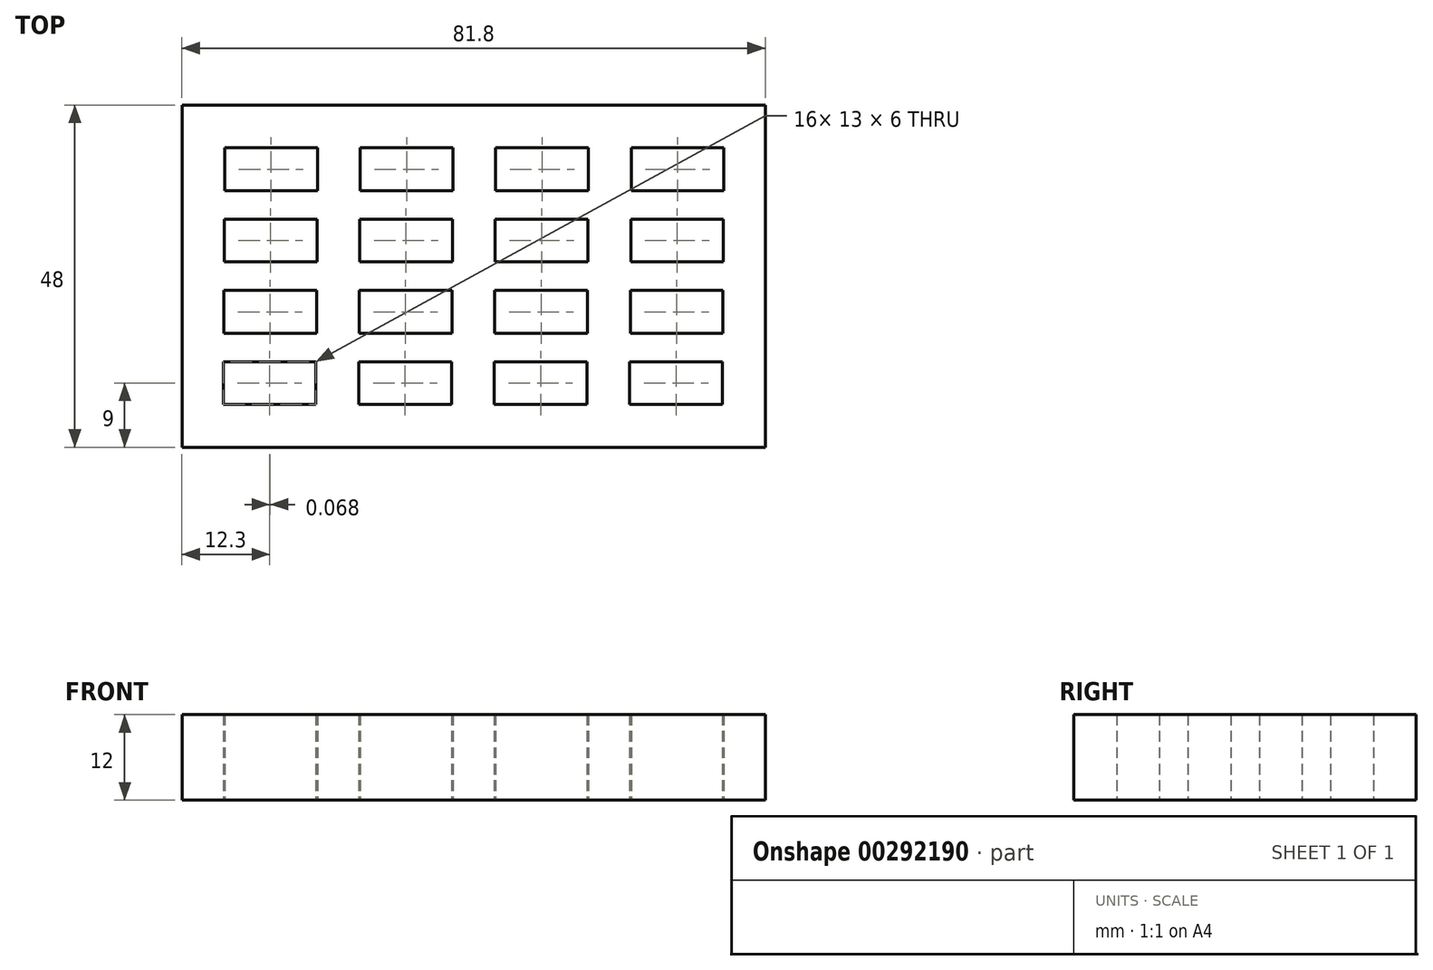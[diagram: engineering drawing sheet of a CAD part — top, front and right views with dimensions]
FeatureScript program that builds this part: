
annotation { "Feature Type Name" : "Feature", "Feature Type Description" : "" }
export const myFeature = defineFeature(function(context is Context, id is Id, definition is map)
    precondition{}
    {
        {
            var Q0;
            Q0=qCreatedBy(makeId("Top.planeOp"),FACE);
            var sketch = newSketch(context, id + "F0", { "sketchPlane" : qUnion([Q0])});
            skLineSegment(sketch, "E0.bottom", {"start": v(6.5, 3) * mm, "end": v(-6.5, 3) * mm});
            skLineSegment(sketch, "E0.top", {"start": v(6.5, -3) * mm, "end": v(-6.5, -3) * mm});
            skLineSegment(sketch, "E0.left", {"start": v(6.5, 3) * mm, "end": v(6.5, -3) * mm});
            skLineSegment(sketch, "E0.right", {"start": v(-6.5, 3) * mm, "end": v(-6.5, -3) * mm});
            skPoint(sketch, "E0.middle", {"position": v(0, 0) * mm});
            skLineSegment(sketch, "E1.0.1.0", {"start": v(6.57, 13) * mm, "end": v(-6.43, 13) * mm});
            skLineSegment(sketch, "E1.0.1.1", {"start": v(-6.43, 13) * mm, "end": v(-6.43, 7) * mm});
            skLineSegment(sketch, "E1.0.1.2", {"start": v(6.57, 7) * mm, "end": v(-6.43, 7) * mm});
            skLineSegment(sketch, "E1.0.1.3", {"start": v(6.57, 13) * mm, "end": v(6.57, 7) * mm});
            skPoint(sketch, "E1.0.1.4", {"position": v(0.07, 10) * mm});
            skLineSegment(sketch, "E1.0.2.0", {"start": v(6.64, 23) * mm, "end": v(-6.36, 23) * mm});
            skLineSegment(sketch, "E1.0.2.1", {"start": v(-6.36, 23) * mm, "end": v(-6.36, 17) * mm});
            skLineSegment(sketch, "E1.0.2.2", {"start": v(6.64, 17) * mm, "end": v(-6.36, 17) * mm});
            skLineSegment(sketch, "E1.0.2.3", {"start": v(6.64, 23) * mm, "end": v(6.64, 17) * mm});
            skPoint(sketch, "E1.0.2.4", {"position": v(0.14, 20) * mm});
            skLineSegment(sketch, "E1.0.3.0", {"start": v(6.7, 33) * mm, "end": v(-6.3, 33) * mm});
            skLineSegment(sketch, "E1.0.3.1", {"start": v(-6.3, 33) * mm, "end": v(-6.3, 27) * mm});
            skLineSegment(sketch, "E1.0.3.2", {"start": v(6.7, 27) * mm, "end": v(-6.3, 27) * mm});
            skLineSegment(sketch, "E1.0.3.3", {"start": v(6.7, 33) * mm, "end": v(6.7, 27) * mm});
            skPoint(sketch, "E1.0.3.4", {"position": v(0.2, 30) * mm});
            skLineSegment(sketch, "E1.1.0.0", {"start": v(25.5, 3) * mm, "end": v(12.5, 3) * mm});
            skLineSegment(sketch, "E1.1.0.1", {"start": v(12.5, 3) * mm, "end": v(12.5, -3) * mm});
            skLineSegment(sketch, "E1.1.0.2", {"start": v(25.5, -3) * mm, "end": v(12.5, -3) * mm});
            skLineSegment(sketch, "E1.1.0.3", {"start": v(25.5, 3) * mm, "end": v(25.5, -3) * mm});
            skPoint(sketch, "E1.1.0.4", {"position": v(19, 0) * mm});
            skLineSegment(sketch, "E1.1.1.0", {"start": v(25.57, 13) * mm, "end": v(12.57, 13) * mm});
            skLineSegment(sketch, "E1.1.1.1", {"start": v(12.57, 13) * mm, "end": v(12.57, 7) * mm});
            skLineSegment(sketch, "E1.1.1.2", {"start": v(25.57, 7) * mm, "end": v(12.57, 7) * mm});
            skLineSegment(sketch, "E1.1.1.3", {"start": v(25.57, 13) * mm, "end": v(25.57, 7) * mm});
            skPoint(sketch, "E1.1.1.4", {"position": v(19.07, 10) * mm});
            skLineSegment(sketch, "E1.1.2.0", {"start": v(25.64, 23) * mm, "end": v(12.64, 23) * mm});
            skLineSegment(sketch, "E1.1.2.1", {"start": v(12.64, 23) * mm, "end": v(12.64, 17) * mm});
            skLineSegment(sketch, "E1.1.2.2", {"start": v(25.64, 17) * mm, "end": v(12.64, 17) * mm});
            skLineSegment(sketch, "E1.1.2.3", {"start": v(25.64, 23) * mm, "end": v(25.64, 17) * mm});
            skPoint(sketch, "E1.1.2.4", {"position": v(19.14, 20) * mm});
            skLineSegment(sketch, "E1.1.3.0", {"start": v(25.7, 33) * mm, "end": v(12.7, 33) * mm});
            skLineSegment(sketch, "E1.1.3.1", {"start": v(12.7, 33) * mm, "end": v(12.7, 27) * mm});
            skLineSegment(sketch, "E1.1.3.2", {"start": v(25.7, 27) * mm, "end": v(12.7, 27) * mm});
            skLineSegment(sketch, "E1.1.3.3", {"start": v(25.7, 33) * mm, "end": v(25.7, 27) * mm});
            skPoint(sketch, "E1.1.3.4", {"position": v(19.2, 30) * mm});
            skLineSegment(sketch, "E1.2.0.0", {"start": v(44.5, 3) * mm, "end": v(31.5, 3) * mm});
            skLineSegment(sketch, "E1.2.0.1", {"start": v(31.5, 3) * mm, "end": v(31.5, -3) * mm});
            skLineSegment(sketch, "E1.2.0.2", {"start": v(44.5, -3) * mm, "end": v(31.5, -3) * mm});
            skLineSegment(sketch, "E1.2.0.3", {"start": v(44.5, 3) * mm, "end": v(44.5, -3) * mm});
            skPoint(sketch, "E1.2.0.4", {"position": v(38, 0) * mm});
            skLineSegment(sketch, "E1.2.1.0", {"start": v(44.57, 13) * mm, "end": v(31.57, 13) * mm});
            skLineSegment(sketch, "E1.2.1.1", {"start": v(31.57, 13) * mm, "end": v(31.57, 7) * mm});
            skLineSegment(sketch, "E1.2.1.2", {"start": v(44.57, 7) * mm, "end": v(31.57, 7) * mm});
            skLineSegment(sketch, "E1.2.1.3", {"start": v(44.57, 13) * mm, "end": v(44.57, 7) * mm});
            skPoint(sketch, "E1.2.1.4", {"position": v(38.07, 10) * mm});
            skLineSegment(sketch, "E1.2.2.0", {"start": v(44.64, 23) * mm, "end": v(31.64, 23) * mm});
            skLineSegment(sketch, "E1.2.2.1", {"start": v(31.64, 23) * mm, "end": v(31.64, 17) * mm});
            skLineSegment(sketch, "E1.2.2.2", {"start": v(44.64, 17) * mm, "end": v(31.64, 17) * mm});
            skLineSegment(sketch, "E1.2.2.3", {"start": v(44.64, 23) * mm, "end": v(44.64, 17) * mm});
            skPoint(sketch, "E1.2.2.4", {"position": v(38.14, 20) * mm});
            skLineSegment(sketch, "E1.2.3.0", {"start": v(44.7, 33) * mm, "end": v(31.7, 33) * mm});
            skLineSegment(sketch, "E1.2.3.1", {"start": v(31.7, 33) * mm, "end": v(31.7, 27) * mm});
            skLineSegment(sketch, "E1.2.3.2", {"start": v(44.7, 27) * mm, "end": v(31.7, 27) * mm});
            skLineSegment(sketch, "E1.2.3.3", {"start": v(44.7, 33) * mm, "end": v(44.7, 27) * mm});
            skPoint(sketch, "E1.2.3.4", {"position": v(38.2, 30) * mm});
            skLineSegment(sketch, "E1.3.0.0", {"start": v(63.5, 3) * mm, "end": v(50.5, 3) * mm});
            skLineSegment(sketch, "E1.3.0.1", {"start": v(50.5, 3) * mm, "end": v(50.5, -3) * mm});
            skLineSegment(sketch, "E1.3.0.2", {"start": v(63.5, -3) * mm, "end": v(50.5, -3) * mm});
            skLineSegment(sketch, "E1.3.0.3", {"start": v(63.5, 3) * mm, "end": v(63.5, -3) * mm});
            skPoint(sketch, "E1.3.0.4", {"position": v(57, 0) * mm});
            skLineSegment(sketch, "E1.3.1.0", {"start": v(63.57, 13) * mm, "end": v(50.57, 13) * mm});
            skLineSegment(sketch, "E1.3.1.1", {"start": v(50.57, 13) * mm, "end": v(50.57, 7) * mm});
            skLineSegment(sketch, "E1.3.1.2", {"start": v(63.57, 7) * mm, "end": v(50.57, 7) * mm});
            skLineSegment(sketch, "E1.3.1.3", {"start": v(63.57, 13) * mm, "end": v(63.57, 7) * mm});
            skPoint(sketch, "E1.3.1.4", {"position": v(57.07, 10) * mm});
            skLineSegment(sketch, "E1.3.2.0", {"start": v(63.64, 23) * mm, "end": v(50.64, 23) * mm});
            skLineSegment(sketch, "E1.3.2.1", {"start": v(50.64, 23) * mm, "end": v(50.64, 17) * mm});
            skLineSegment(sketch, "E1.3.2.2", {"start": v(63.64, 17) * mm, "end": v(50.64, 17) * mm});
            skLineSegment(sketch, "E1.3.2.3", {"start": v(63.64, 23) * mm, "end": v(63.64, 17) * mm});
            skPoint(sketch, "E1.3.2.4", {"position": v(57.14, 20) * mm});
            skLineSegment(sketch, "E1.3.3.0", {"start": v(63.7, 33) * mm, "end": v(50.7, 33) * mm});
            skLineSegment(sketch, "E1.3.3.1", {"start": v(50.7, 33) * mm, "end": v(50.7, 27) * mm});
            skLineSegment(sketch, "E1.3.3.2", {"start": v(63.7, 27) * mm, "end": v(50.7, 27) * mm});
            skLineSegment(sketch, "E1.3.3.3", {"start": v(63.7, 33) * mm, "end": v(63.7, 27) * mm});
            skPoint(sketch, "E1.3.3.4", {"position": v(57.2, 30) * mm});
            skLineSegment(sketch, "E1.direction1", {"start": v(-6.5, -3) * mm, "end": v(12.5, -3) * mm, "construction": true});
            skLineSegment(sketch, "E1.direction2", {"start": v(-6.5, -3) * mm, "end": v(-6.43, 7) * mm, "construction": true});
            skSolve(sketch);
        }
        {
            var Q0;
            Q0=qCreatedBy(makeId("Top.planeOp"),FACE);
            var sketch = newSketch(context, id + "F1", { "sketchPlane" : qUnion([Q0])});
            skLineSegment(sketch, "E2.bottom", {"start": v(-12.3, -9) * mm, "end": v(69.5, -9) * mm});
            skLineSegment(sketch, "E2.top", {"start": v(-12.3, 39) * mm, "end": v(69.5, 39) * mm});
            skLineSegment(sketch, "E2.left", {"start": v(-12.3, -9) * mm, "end": v(-12.3, 39) * mm});
            skLineSegment(sketch, "E2.right", {"start": v(69.5, -9) * mm, "end": v(69.5, 39) * mm});
            skSolve(sketch);
        }
        {
            var Q0;
            Q0=makeQuery(id+"F1.imprint","IMPRINT",FACE,{"disambiguationData":[TD([[makeQuery(id+"F1.imprint","IMPRINT",EDGE,{"derivedFrom":sQuery(id+"F1.wireOp",EDGE,"E2.bottom")}),1.0]])]});
            extrude(context, id + "F2", {"entities" : qUnion([Q0]), "depth" : 12 * mm});
        }
        {
            var Q0;
            Q0 = qSketchRegion(id + "F0", true);
            extrude(context, id + "F3", {"entities" : qUnion([Q0]), "operationType" : NewBodyOperationType.REMOVE, "endBound" : BoundingType.THROUGH_ALL, "depth" : 25 * mm});
        }
    });
